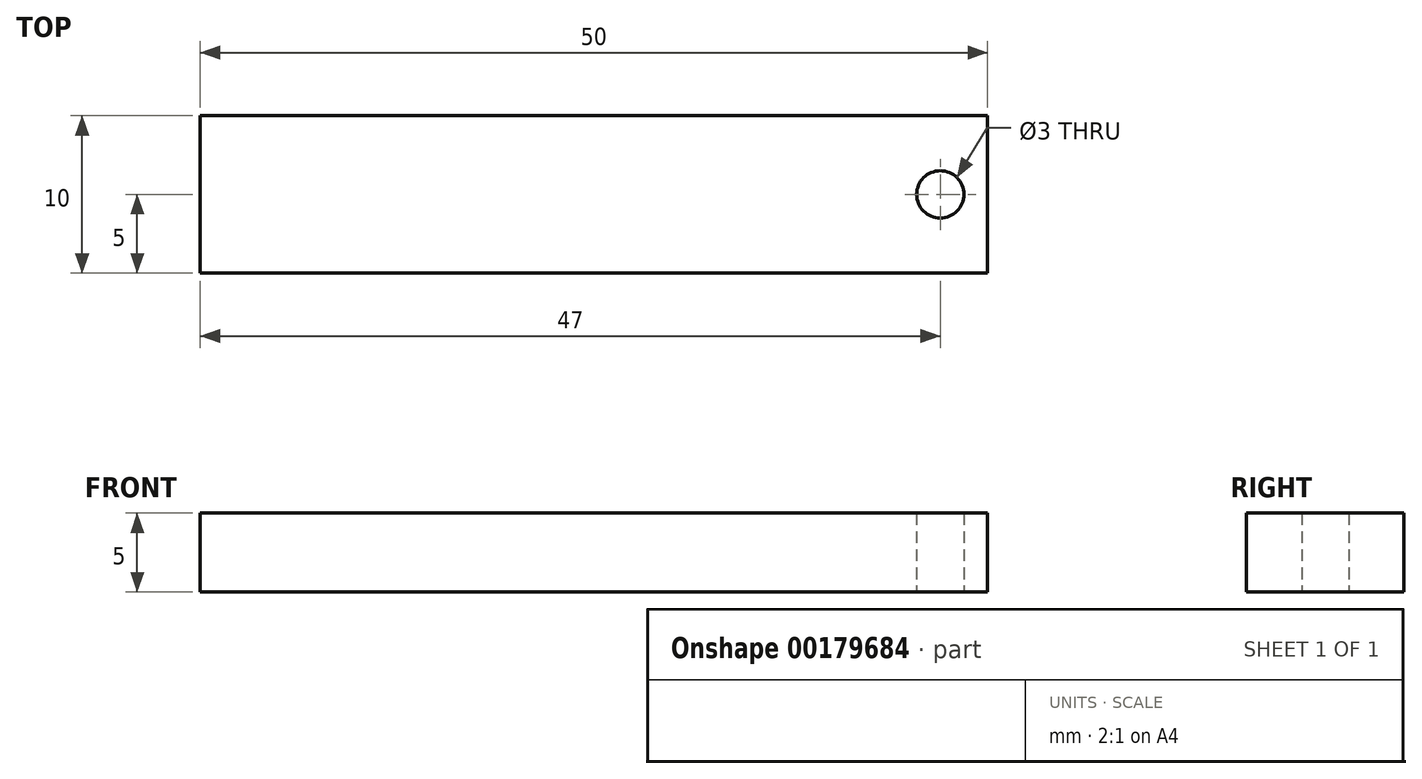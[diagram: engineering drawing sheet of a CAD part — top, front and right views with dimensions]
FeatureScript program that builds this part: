
annotation { "Feature Type Name" : "Feature", "Feature Type Description" : "" }
export const myFeature = defineFeature(function(context is Context, id is Id, definition is map)
    precondition{}
    {
        {
            var Q0;
            Q0=qCreatedBy(makeId("Top.planeOp"),FACE);
            var sketch = newSketch(context, id + "F0", { "sketchPlane" : qUnion([Q0])});
            skLineSegment(sketch, "E0.bottom", {"start": v(25, 5) * mm, "end": v(-25, 5) * mm});
            skLineSegment(sketch, "E0.top", {"start": v(25, -5) * mm, "end": v(-25, -5) * mm});
            skLineSegment(sketch, "E0.left", {"start": v(25, 5) * mm, "end": v(25, -5) * mm});
            skLineSegment(sketch, "E0.right", {"start": v(-25, 5) * mm, "end": v(-25, -5) * mm});
            skPoint(sketch, "E0.middle", {"position": v(0, 0) * mm});
            skCircle(sketch, "E1", {"center": v(22, 0) * mm, "radius": 1.5 * mm});
            skSolve(sketch);
        }
        {
            var Q0;
            Q0 = qSketchRegion(id + "F0", true);
            extrude(context, id + "F1", {"entities" : qUnion([Q0]), "depth" : 5 * mm});
        }
    });
